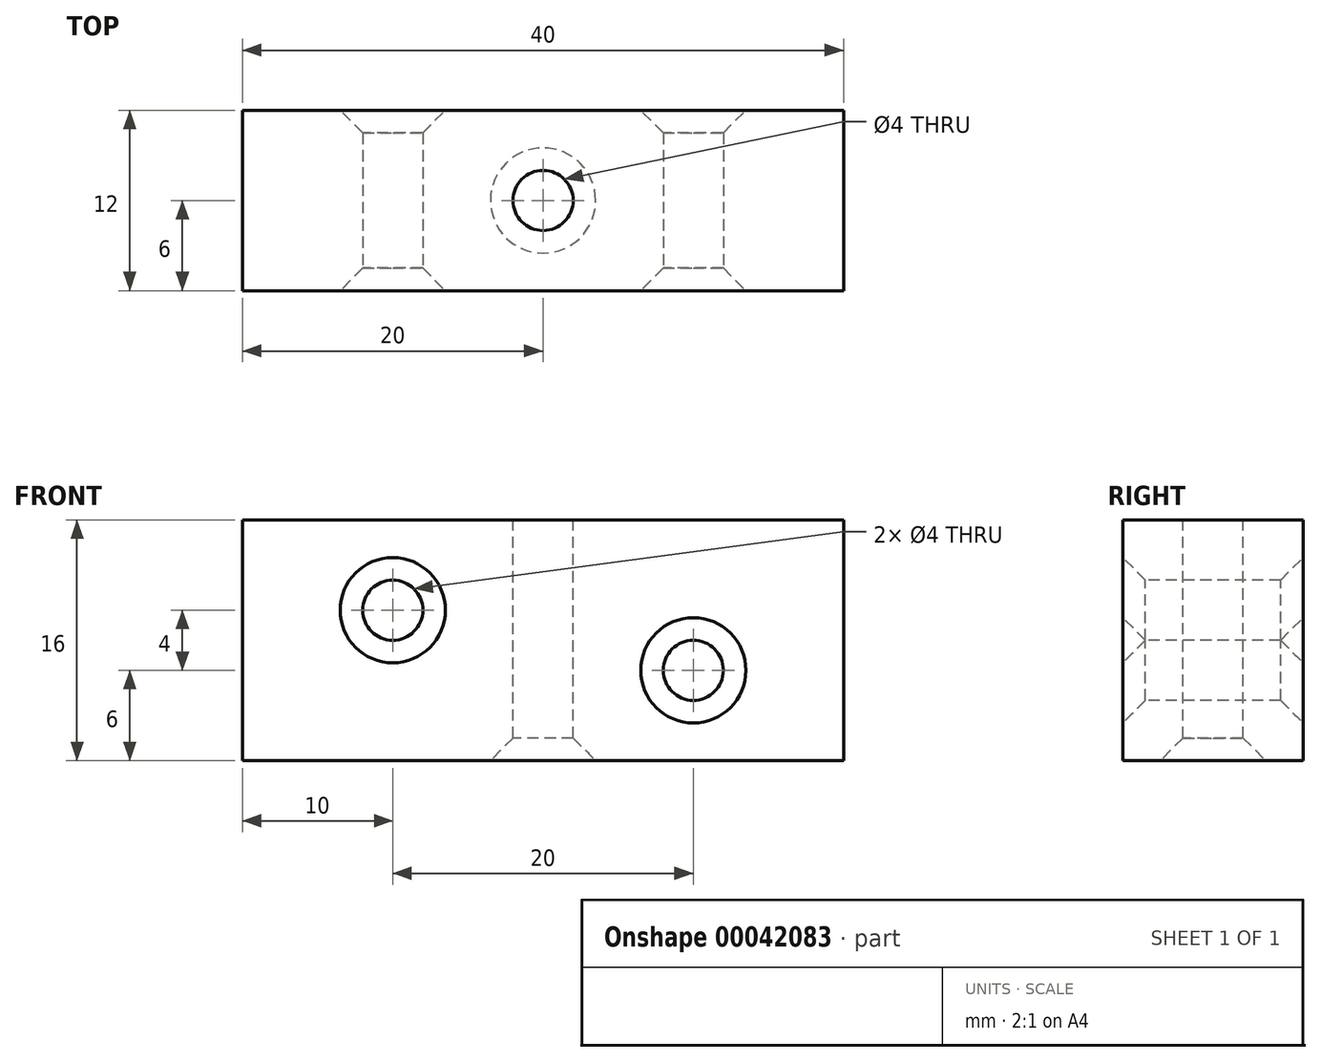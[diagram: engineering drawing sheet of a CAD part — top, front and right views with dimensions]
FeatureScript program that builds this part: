
annotation { "Feature Type Name" : "Feature", "Feature Type Description" : "" }
export const myFeature = defineFeature(function(context is Context, id is Id, definition is map)
    precondition{}
    {
        {
            var Q0;
            Q0=qCreatedBy(makeId("Front.planeOp"),FACE);
            var sketch = newSketch(context, id + "F0", { "sketchPlane" : qUnion([Q0])});
            skLineSegment(sketch, "E0.rect.bottom", {"start": v(20, -8) * mm, "end": v(-20, -8) * mm});
            skLineSegment(sketch, "E0.rect.top", {"start": v(20, 8) * mm, "end": v(-20, 8) * mm});
            skLineSegment(sketch, "E0.rect.left", {"start": v(20, -8) * mm, "end": v(20, 8) * mm});
            skLineSegment(sketch, "E0.rect.right", {"start": v(-20, -8) * mm, "end": v(-20, 8) * mm});
            skPoint(sketch, "E0.rect.middle", {"position": v(0, 0) * mm});
            skCircle(sketch, "E1", {"center": v(-10, 2) * mm, "radius": 2 * mm});
            skLineSegment(sketch, "E2", {"start": v(0, 19.94) * mm, "end": v(0, -22.65) * mm, "construction": true});
            skPoint(sketch, "E2.endSnap0", {"position": v(0, -8) * mm});
            skCircle(sketch, "E3.MirrorC", {"center": v(10, -2) * mm, "radius": 2 * mm});
            skSolve(sketch);
        }
        {
            var Q0;
            Q0=makeQuery(id+"F0.imprint","IMPRINT",FACE,{"disambiguationData":[TD([[makeQuery(id+"F0.imprint","IMPRINT",EDGE,{"derivedFrom":sQuery(id+"F0.wireOp",EDGE,"E0.rect.bottom")}),-1.0]])]});
            extrude(context, id + "F1", {"entities" : qUnion([Q0]), "oppositeDirection" : true, "depth" : 12 * mm});
        }
        {
            var Q0;
            Q0=makeQuery(id+"F1.opExtrude","SWEPT_FACE",FACE,{"disambiguationData":[OSD([sQuery(id+"F0.wireOp",EDGE,"E0.rect.top")])]});
            var sketch = newSketch(context, id + "F2", { "sketchPlane" : qUnion([Q0])});
            skCircle(sketch, "E4", {"center": v(0, 6) * mm, "radius": 2 * mm});
            skSolve(sketch);
        }
        {
            var Q0;
            Q0=makeQuery(id+"F2.imprint","IMPRINT",FACE,{"disambiguationData":[TD([[makeQuery(id+"F2.imprint","IMPRINT",EDGE,{"derivedFrom":sQuery(id+"F2.wireOp",EDGE,"E4")}),1.0]])]});
            extrude(context, id + "F3", {"entities" : qUnion([Q0]), "operationType" : NewBodyOperationType.REMOVE, "endBound" : BoundingType.THROUGH_ALL, "oppositeDirection" : true, "depth" : 25 * mm});
        }
        {
            var Q0;
            Q0=makeQuery(id+"F1.opExtrude","CAP_EDGE",EDGE,{"disambiguationData":[OSD([sQuery(id+"F0.wireOp",EDGE,"E1")])],"isStart":false});
            var Q1;
            Q1=makeQuery(id+"F1.opExtrude","CAP_EDGE",EDGE,{"disambiguationData":[OSD([sQuery(id+"F0.wireOp",EDGE,"E3.MirrorC")])],"isStart":false});
            var Q2;
            Q2=makeQuery(id+"F1.opExtrude","CAP_EDGE",EDGE,{"disambiguationData":[OSD([sQuery(id+"F0.wireOp",EDGE,"E1")])],"isStart":true});
            var Q3;
            Q3=makeQuery(id+"F1.opExtrude","CAP_EDGE",EDGE,{"disambiguationData":[OSD([sQuery(id+"F0.wireOp",EDGE,"E3.MirrorC")])],"isStart":true});
            var Q4;
            Q4=makeQuery(id+"F3.boolean.opBoolean","COPY",EDGE,{"derivedFrom":makeQuery(id+"F3.opExtrude","CAP_EDGE",EDGE,{"disambiguationData":[OSD([sQuery(id+"F2.wireOp",EDGE,"E4")])],"isStart":true})});
            var Q5;
            Q5=makeQuery(id+"F3.boolean.opBoolean","INTERSECT",EDGE,{"derivedFrom":[makeQuery(id+"F1.opExtrude","SWEPT_FACE",FACE,{"disambiguationData":[OSD([sQuery(id+"F0.wireOp",EDGE,"E0.rect.bottom")])]}),makeQuery(id+"F3.opExtrude","SWEPT_FACE",FACE,{"disambiguationData":[OSD([sQuery(id+"F2.wireOp",EDGE,"E4")])]})]});
            chamfer(context, id + "F4", {"entities" : qUnion([Q0, Q1, Q2, Q3, Q4, Q5]), "width" : 1.5 * mm});
        }
    });
